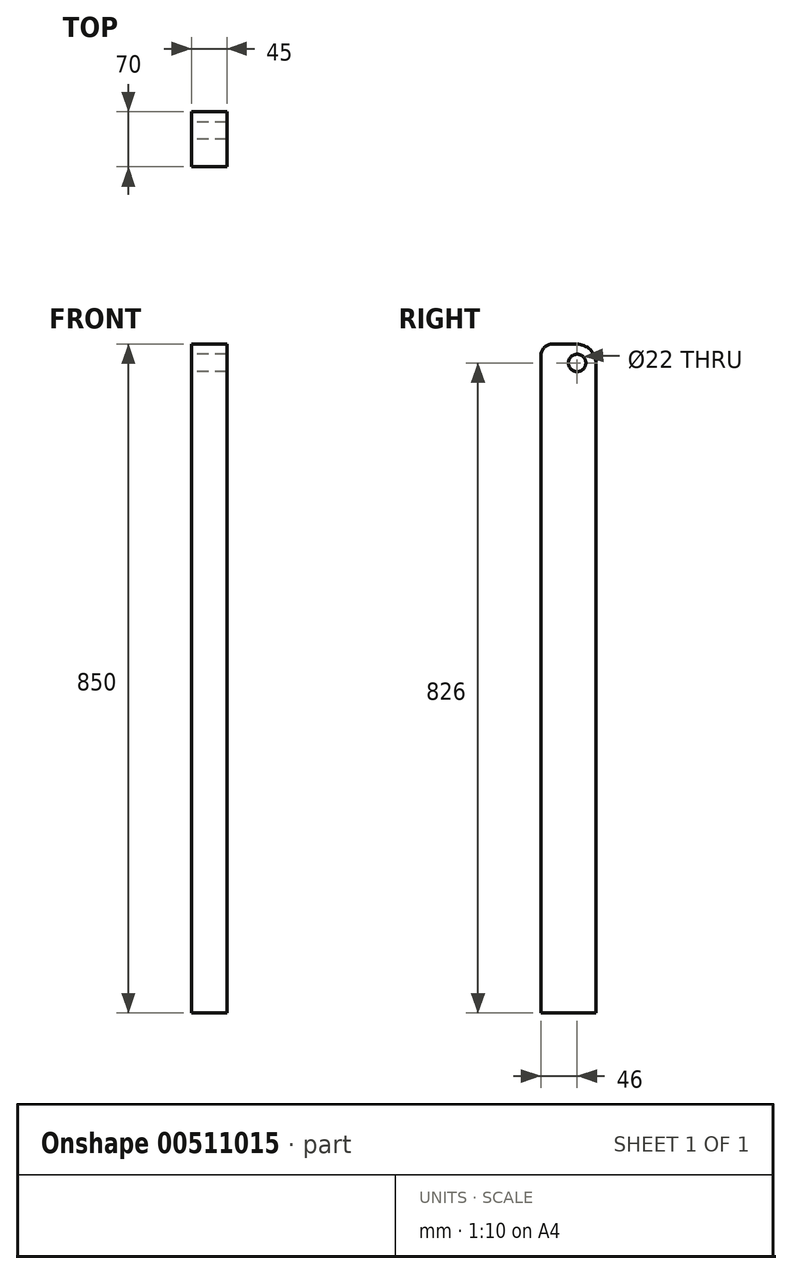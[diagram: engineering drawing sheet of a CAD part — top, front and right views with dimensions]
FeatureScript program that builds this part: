
annotation { "Feature Type Name" : "Feature", "Feature Type Description" : "" }
export const myFeature = defineFeature(function(context is Context, id is Id, definition is map)
    precondition{}
    {
        {
            var Q0;
            Q0=qCreatedBy(makeId("Front.planeOp"),FACE);
            var sketch = newSketch(context, id + "F0", { "sketchPlane" : qUnion([Q0])});
            skLineSegment(sketch, "E0.bottom", {"start": v(0, 0) * mm, "end": v(45, 0) * mm});
            skLineSegment(sketch, "E0.top", {"start": v(0, -850) * mm, "end": v(45, -850) * mm});
            skLineSegment(sketch, "E0.left", {"start": v(0, 0) * mm, "end": v(0, -850) * mm});
            skLineSegment(sketch, "E0.right", {"start": v(45, 0) * mm, "end": v(45, -850) * mm});
            skSolve(sketch);
        }
        {
            var Q0;
            Q0=qSketchRegion(id+"F0",true);
            extrude(context, id + "F1", {"entities" : qUnion([Q0]), "depth" : 70 * mm});
        }
        {
            var Q0;
            Q0=makeQuery(id+"F1.opExtrude","SWEPT_FACE",FACE,{"disambiguationData":[OSD([sQuery(id+"F0.wireOp",EDGE,"E0.left")])]});
            var sketch = newSketch(context, id + "F2", { "sketchPlane" : qUnion([Q0])});
            skCircle(sketch, "E1", {"center": v(24, -24) * mm, "radius": 11 * mm});
            skSolve(sketch);
        }
        {
            var Q0;
            Q0=qSketchRegion(id+"F2",true);
            extrude(context, id + "F3", {"entities" : qUnion([Q0]), "operationType" : NewBodyOperationType.REMOVE, "endBound" : BoundingType.THROUGH_ALL, "oppositeDirection" : true, "depth" : 25 * mm});
        }
        {
            var Q0;
            Q0=makeQuery(id+"F1.opExtrude","CAP_EDGE",EDGE,{"disambiguationData":[OSD([sQuery(id+"F0.wireOp",EDGE,"E0.bottom")])],"isStart":true});
            fillet(context, id + "F4", {"entities" : qUnion([Q0]), "radius" : 25 * mm, "tangentPropagation" : true, "allowEdgeOverflow" : false});
        }
        {
            var Q0;
            Q0=makeQuery(id+"F1.opExtrude","CAP_EDGE",EDGE,{"disambiguationData":[OSD([sQuery(id+"F0.wireOp",EDGE,"E0.bottom")])],"isStart":false});
            fillet(context, id + "F5", {"entities" : qUnion([Q0]), "radius" : 15 * mm, "tangentPropagation" : true, "allowEdgeOverflow" : false});
        }
    });
